# Revit family: Seals-Shelters_Serco_IDS-HC-Ironside
name_source: partatom
category: Generic Models
units: mm (PartAtom-declared; Revit-internal decimal feet)

## family parameters
Always vertical = Yes
Can host rebar = No
Cut with Voids When Loaded = No
Host = Wall
Maintain Annotation Orientation = No
Part Type = Normal
Room Calculation Point = No
Round Connector Dimension = Use Diameter
Shared = No

## types (6) — shared parameters
Default Elevation = 0' - 0"
Description = Foam Dock Seal
DropCurtain = 2' - 0"
Manufacturer = Entrematic
Model = IDS-HC Ironside/ADS-HC Armorguard
Projection = 0' - 10"
URL = https://www.entrematic.us

## per-type parameters (varying)
| type | Opening | SidePadHeight | Width |
| 8'x10' Door | 7' - 6" | 10' - 0" | 9' - 6" |
| 8.5'x10' Door | 7' - 8" | 10' - 0" | 10' - 0" |
| 9'x10' Door | 7' - 10" | 10' - 0" | 10' - 7" |
| 8'x12' Door | 7' - 6" | 12' - 0" | 9' - 6" |
| 8.5'x12' Door | 7' - 8" | 12' - 0" | 10' - 0" |
| 9'x12' Door | 7' - 10" | 12' - 0" | 10' - 7" |

## geometry (parser evidence)
native form markers: Sweep x3
no freeform markers — native parametric forms only
